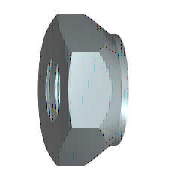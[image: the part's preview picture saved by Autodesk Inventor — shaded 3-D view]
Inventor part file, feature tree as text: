
AUTODESK INVENTOR PART (.ipt)
format: ipt  version: 2014 SP1 (Build 180222100, 222)  size: 179,712 bytes
history: native  units: mm (DEFAULTED — no unit token found)
features: sketch x3, hole x1, chamfer x1, other x1, plane x1
ambient origin geometry x7: Origin, YZ Plane, XZ Plane, X Axis, Y Axis, Z Axis, Center Point
bodies: Solid1 (feature_tree), Body (feature_tree)
feature tree (7):
  hole  "Thread"  [1 undecoded]
  chamfer  "Chamfer3"  Distance=7.9375mm
  other  "Work Axis1"
  plane  "Work Plane1"
  sketch  "Sketch1"  dims[d0=9.165436mm d1=4.3434mm]
  sketch  "Sketch3"  dims[d3=30.0deg d5=7.9375mm d6=6.746875mm d7=90.0deg d8=60.0deg d9=1.905mm d24=2.6416mm d25=6.0mm d26=4.0mm d27=2.0mm d28=14.3117mm d29=8.0mm d30=20.594885mm d10=0.42963mm d11=30.0deg d12=0.42963mm d13=30.0deg d14=0.0mm d38=0.0mm d39=0.42963mm d40=0.42963mm d41=0.0mm d42=0.0mm]
  sketch  "Sketch2"  dims[d2=0.0mm]
note: 1 required parameter value undecoded (feature->parameter linkage not recoverable at this tier; creation-order binding heuristic only, values carry confidence <= 0.55)
